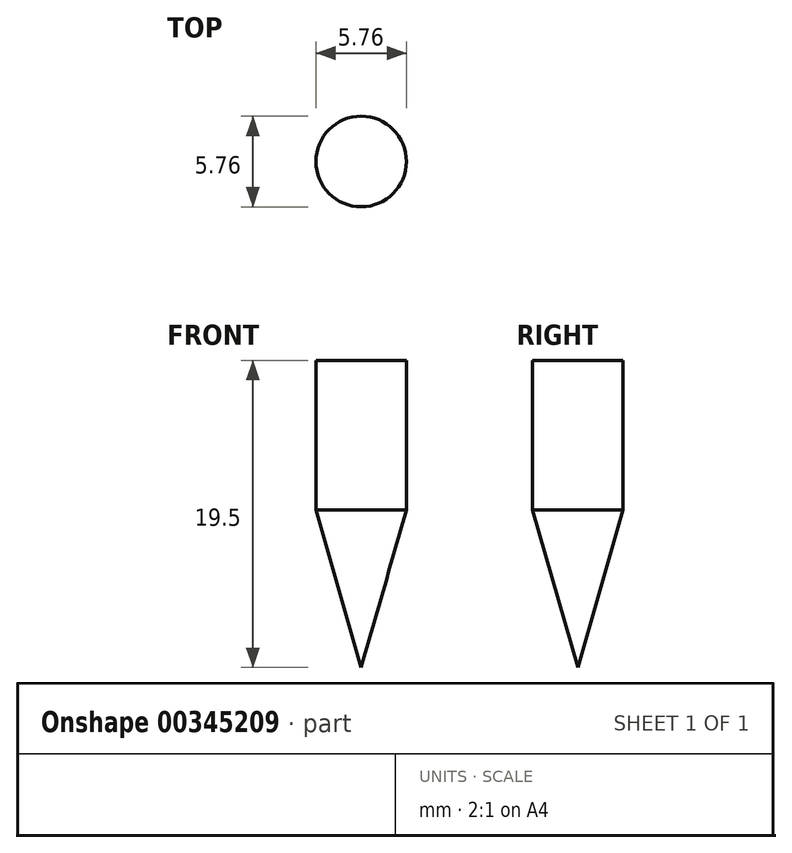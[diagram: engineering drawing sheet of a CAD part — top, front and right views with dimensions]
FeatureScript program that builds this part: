
annotation { "Feature Type Name" : "Feature", "Feature Type Description" : "" }
export const myFeature = defineFeature(function(context is Context, id is Id, definition is map)
    precondition{}
    {
        {
            var Q0;
            Q0=qCreatedBy(makeId("Front.planeOp"),FACE);
            var sketch = newSketch(context, id + "F0", { "sketchPlane" : qUnion([Q0])});
            skLineSegment(sketch, "E0", {"start": v(0, 0) * mm, "end": v(2.87, 0) * mm});
            skLineSegment(sketch, "E1", {"start": v(0, 0) * mm, "end": v(0, -19.5) * mm});
            skLineSegment(sketch, "E2", {"start": v(2.87, 0) * mm, "end": v(2.87, -9.5) * mm});
            skLineSegment(sketch, "E3", {"start": v(2.87, -9.5) * mm, "end": v(0, -19.5) * mm});
            skSolve(sketch);
        }
        {
            var Q0;
            Q0=makeQuery(id+"F0.imprint","IMPRINT",FACE,{"disambiguationData":[TD([[makeQuery(id+"F0.imprint","IMPRINT",EDGE,{"derivedFrom":sQuery(id+"F0.wireOp",EDGE,"E0")}),-1.0]])]});
            var Q1;
            Q1=sQuery(id+"F0.wireOp",EDGE,"E1");
            revolve(context, id + "F1", {"entities" : qUnion([Q0]), "axis" : qUnion([Q1]), "revolveType" : RevolveType.FULL});
        }
    });
